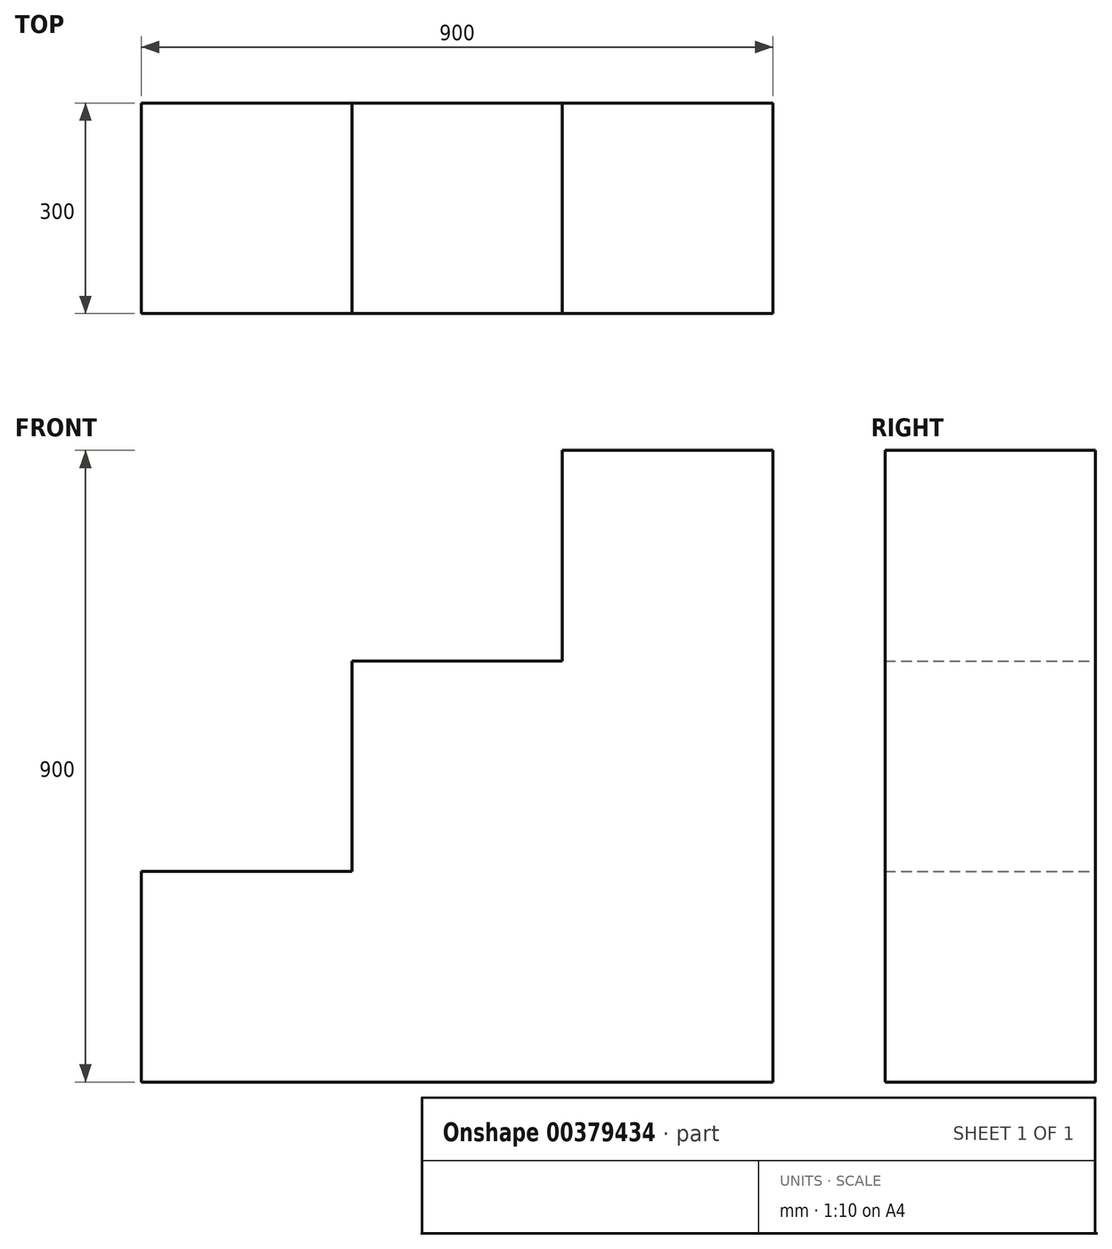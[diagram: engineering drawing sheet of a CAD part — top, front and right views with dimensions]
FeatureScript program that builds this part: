
annotation { "Feature Type Name" : "Feature", "Feature Type Description" : "" }
export const myFeature = defineFeature(function(context is Context, id is Id, definition is map)
    precondition{}
    {
        {
            var Q0;
            Q0=qCreatedBy(makeId("Front.planeOp"),FACE);
            var sketch = newSketch(context, id + "F0", { "sketchPlane" : qUnion([Q0])});
            skLineSegment(sketch, "E0", {"start": v(392.42, -466.55) * mm, "end": v(392.42, 433.45) * mm});
            skLineSegment(sketch, "E1", {"start": v(392.42, 433.45) * mm, "end": v(92.42, 433.45) * mm});
            skLineSegment(sketch, "E2", {"start": v(92.42, 433.45) * mm, "end": v(92.42, 133.45) * mm});
            skLineSegment(sketch, "E3", {"start": v(92.42, 133.45) * mm, "end": v(-207.58, 133.45) * mm});
            skLineSegment(sketch, "E4", {"start": v(-207.58, 133.45) * mm, "end": v(-207.58, -166.55) * mm});
            skLineSegment(sketch, "E5", {"start": v(-507.58, -166.55) * mm, "end": v(-507.58, -466.55) * mm});
            skLineSegment(sketch, "E6", {"start": v(-507.58, -466.55) * mm, "end": v(392.42, -466.55) * mm});
            skLineSegment(sketch, "E7", {"start": v(-507.58, -166.55) * mm, "end": v(-207.58, -166.55) * mm});
            skSolve(sketch);
        }
        {
            var Q0;
            Q0 = qSketchRegion(id + "F0", true);
            extrude(context, id + "F1", {"entities" : qUnion([Q0]), "depth" : 300 * mm});
        }
    });
